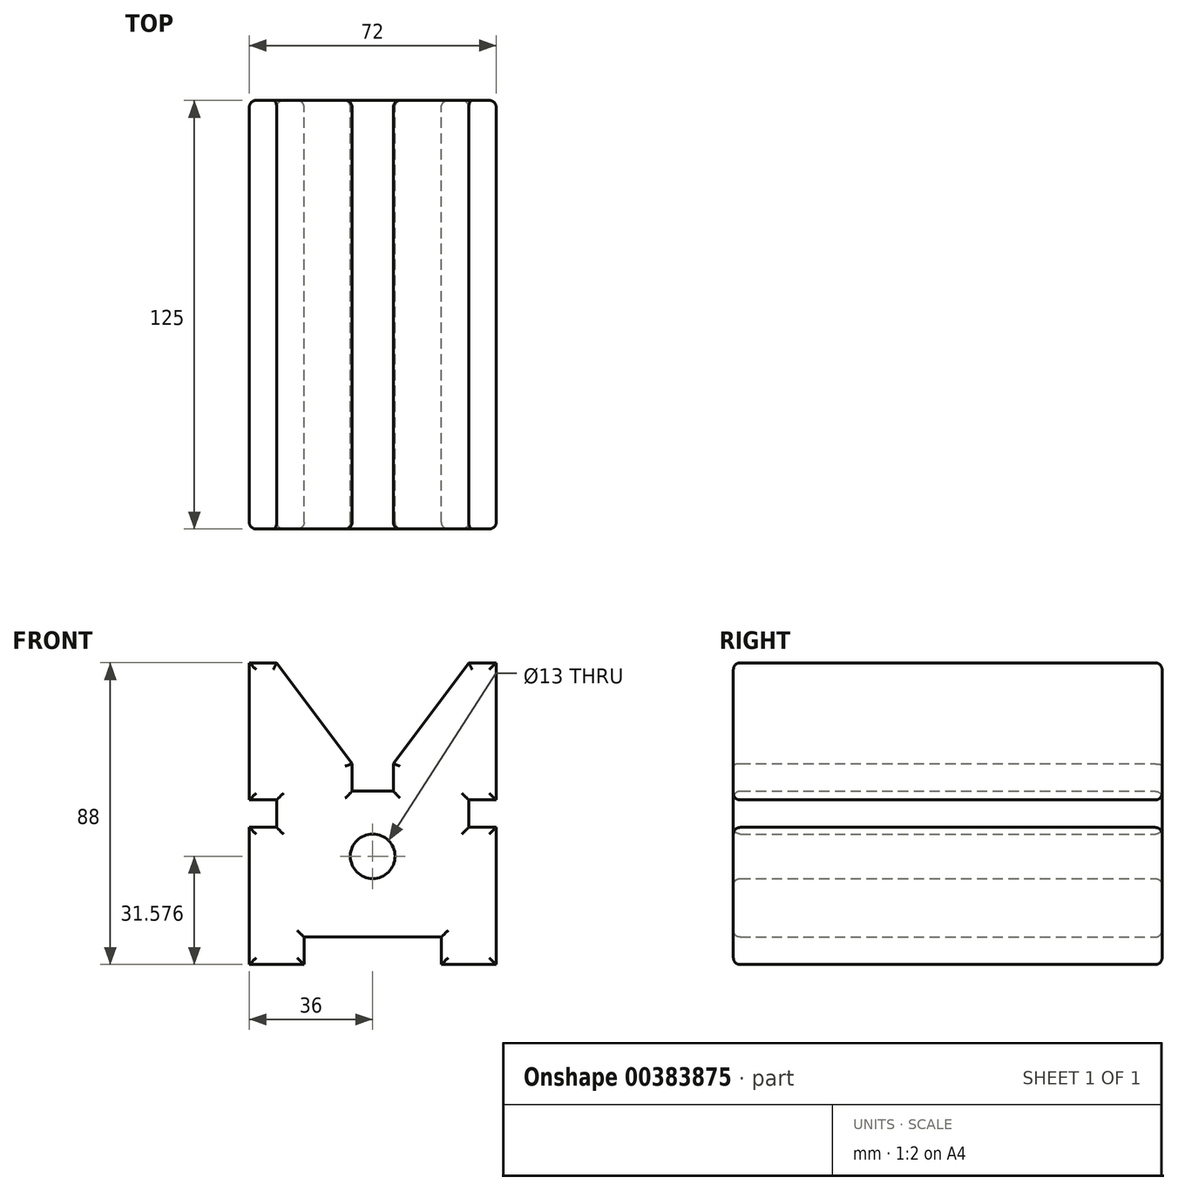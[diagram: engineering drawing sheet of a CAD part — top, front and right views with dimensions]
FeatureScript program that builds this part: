
annotation { "Feature Type Name" : "Feature", "Feature Type Description" : "" }
export const myFeature = defineFeature(function(context is Context, id is Id, definition is map)
    precondition{}
    {
        {
            var Q0;
            Q0=qCreatedBy(makeId("Front.planeOp"),FACE);
            var sketch = newSketch(context, id + "F0", { "sketchPlane" : qUnion([Q0])});
            skLineSegment(sketch, "E0", {"start": v(-16, -17.94) * mm, "end": v(0, -17.94) * mm});
            skLineSegment(sketch, "E1", {"start": v(0, -9.94) * mm, "end": v(0, -17.94) * mm});
            skLineSegment(sketch, "E2", {"start": v(0, -9.94) * mm, "end": v(40, -9.94) * mm});
            skLineSegment(sketch, "E3", {"start": v(40, -9.94) * mm, "end": v(40, -17.94) * mm});
            skLineSegment(sketch, "E4", {"start": v(40, -17.94) * mm, "end": v(56, -17.94) * mm});
            skLineSegment(sketch, "E5", {"start": v(56, -17.94) * mm, "end": v(56, 22.06) * mm});
            skLineSegment(sketch, "E6", {"start": v(56, 22.06) * mm, "end": v(48, 22.06) * mm});
            skLineSegment(sketch, "E7", {"start": v(48, 22.06) * mm, "end": v(48, 30.06) * mm});
            skLineSegment(sketch, "E8", {"start": v(48, 30.06) * mm, "end": v(56, 30.06) * mm});
            skLineSegment(sketch, "E9", {"start": v(56, 30.06) * mm, "end": v(56, 70.06) * mm});
            skLineSegment(sketch, "E10", {"start": v(56, 70.06) * mm, "end": v(48, 70.06) * mm});
            skLineSegment(sketch, "E11", {"start": v(48, 70.06) * mm, "end": v(26, 40.6) * mm});
            skLineSegment(sketch, "E12", {"start": v(26, 40.6) * mm, "end": v(26, 32.6) * mm});
            skLineSegment(sketch, "E13", {"start": v(26, 32.6) * mm, "end": v(14, 32.6) * mm});
            skLineSegment(sketch, "E14", {"start": v(14, 32.6) * mm, "end": v(14, 40.6) * mm});
            skLineSegment(sketch, "E15", {"start": v(14, 40.6) * mm, "end": v(-8, 70.06) * mm});
            skLineSegment(sketch, "E16", {"start": v(-8, 70.06) * mm, "end": v(-16, 70.06) * mm});
            skLineSegment(sketch, "E17", {"start": v(20, 32.6) * mm, "end": v(20, 75.32) * mm});
            skLineSegment(sketch, "E18", {"start": v(20, 75.32) * mm, "end": v(20, -9.94) * mm, "construction": true});
            skCircle(sketch, "E19", {"center": v(20, 13.64) * mm, "radius": 6.5 * mm});
            skLineSegment(sketch, "E20.MirrorCS", {"start": v(-16, 30.06) * mm, "end": v(-16, 70.06) * mm});
            skLineSegment(sketch, "E21.MirrorCS", {"start": v(-16, 70.06) * mm, "end": v(-8, 70.06) * mm});
            skLineSegment(sketch, "E22.MirrorCS", {"start": v(-8, 70.06) * mm, "end": v(14, 40.6) * mm});
            skLineSegment(sketch, "E23.MirrorCS", {"start": v(-8, 30.06) * mm, "end": v(-16, 30.06) * mm});
            skLineSegment(sketch, "E24.MirrorCS", {"start": v(-8, 22.06) * mm, "end": v(-8, 30.06) * mm});
            skLineSegment(sketch, "E25.MirrorCS", {"start": v(-16, 22.06) * mm, "end": v(-8, 22.06) * mm});
            skLineSegment(sketch, "E26.MirrorCS", {"start": v(-16, -17.94) * mm, "end": v(-16, 22.06) * mm});
            skSolve(sketch);
        }
        {
            var Q0;
            Q0=makeQuery(id+"F0.imprint","IMPRINT",FACE,{"disambiguationData":[TD([[makeQuery(id+"F0.imprint","IMPRINT",EDGE,{"derivedFrom":sQuery(id+"F0.wireOp",EDGE,"E0")}),1.0]])]});
            extrude(context, id + "F1", {"entities" : qUnion([Q0]), "depth" : 125 * mm});
        }
        {
            var Q0;
            Q0=makeQuery(id+"F1.opExtrude","CAP_EDGE",EDGE,{"disambiguationData":[OSD([sQuery(id+"F0.wireOp",EDGE,"E20.MirrorCS")])],"isStart":false});
            var Q1;
            Q1=makeQuery(id+"F1.opExtrude","CAP_EDGE",EDGE,{"disambiguationData":[OSD([sQuery(id+"F0.wireOp",EDGE,"E21.MirrorCS")])],"isStart":false});
            var Q2;
            Q2=makeQuery(id+"F1.opExtrude","CAP_EDGE",EDGE,{"disambiguationData":[OSD([sQuery(id+"F0.wireOp",EDGE,"E22.MirrorCS")])],"isStart":false});
            var Q3;
            Q3=makeQuery(id+"F1.opExtrude","CAP_FACE",FACE,{"disambiguationData":[OSD([sQuery(id+"F0.wireOp",EDGE,"E0"),sQuery(id+"F0.wireOp",EDGE,"E1"),sQuery(id+"F0.wireOp",EDGE,"E2"),sQuery(id+"F0.wireOp",EDGE,"E3"),sQuery(id+"F0.wireOp",EDGE,"E4"),sQuery(id+"F0.wireOp",EDGE,"E5"),sQuery(id+"F0.wireOp",EDGE,"E6"),sQuery(id+"F0.wireOp",EDGE,"E7"),sQuery(id+"F0.wireOp",EDGE,"E8"),sQuery(id+"F0.wireOp",EDGE,"E9"),sQuery(id+"F0.wireOp",EDGE,"E10"),sQuery(id+"F0.wireOp",EDGE,"E11"),sQuery(id+"F0.wireOp",EDGE,"E12"),sQuery(id+"F0.wireOp",EDGE,"E13"),sQuery(id+"F0.wireOp",EDGE,"E14"),sQuery(id+"F0.wireOp",EDGE,"E19"),sQuery(id+"F0.wireOp",EDGE,"E20.MirrorCS"),sQuery(id+"F0.wireOp",EDGE,"E21.MirrorCS"),sQuery(id+"F0.wireOp",EDGE,"E22.MirrorCS"),sQuery(id+"F0.wireOp",EDGE,"E23.MirrorCS"),sQuery(id+"F0.wireOp",EDGE,"E24.MirrorCS"),sQuery(id+"F0.wireOp",EDGE,"E25.MirrorCS"),sQuery(id+"F0.wireOp",EDGE,"E26.MirrorCS")])],"isStart":false});
            var Q4;
            Q4=makeQuery(id+"F1.opExtrude","CAP_FACE",FACE,{"disambiguationData":[OSD([sQuery(id+"F0.wireOp",EDGE,"E0"),sQuery(id+"F0.wireOp",EDGE,"E1"),sQuery(id+"F0.wireOp",EDGE,"E2"),sQuery(id+"F0.wireOp",EDGE,"E3"),sQuery(id+"F0.wireOp",EDGE,"E4"),sQuery(id+"F0.wireOp",EDGE,"E5"),sQuery(id+"F0.wireOp",EDGE,"E6"),sQuery(id+"F0.wireOp",EDGE,"E7"),sQuery(id+"F0.wireOp",EDGE,"E8"),sQuery(id+"F0.wireOp",EDGE,"E9"),sQuery(id+"F0.wireOp",EDGE,"E10"),sQuery(id+"F0.wireOp",EDGE,"E11"),sQuery(id+"F0.wireOp",EDGE,"E12"),sQuery(id+"F0.wireOp",EDGE,"E13"),sQuery(id+"F0.wireOp",EDGE,"E14"),sQuery(id+"F0.wireOp",EDGE,"E19"),sQuery(id+"F0.wireOp",EDGE,"E20.MirrorCS"),sQuery(id+"F0.wireOp",EDGE,"E21.MirrorCS"),sQuery(id+"F0.wireOp",EDGE,"E22.MirrorCS"),sQuery(id+"F0.wireOp",EDGE,"E23.MirrorCS"),sQuery(id+"F0.wireOp",EDGE,"E24.MirrorCS"),sQuery(id+"F0.wireOp",EDGE,"E25.MirrorCS"),sQuery(id+"F0.wireOp",EDGE,"E26.MirrorCS")])],"isStart":true});
            fillet(context, id + "F2", {"entities" : qUnion([Q0, Q1, Q2, Q3, Q4]), "radius" : 2 * mm, "tangentPropagation" : true, "allowEdgeOverflow" : false});
        }
    });
